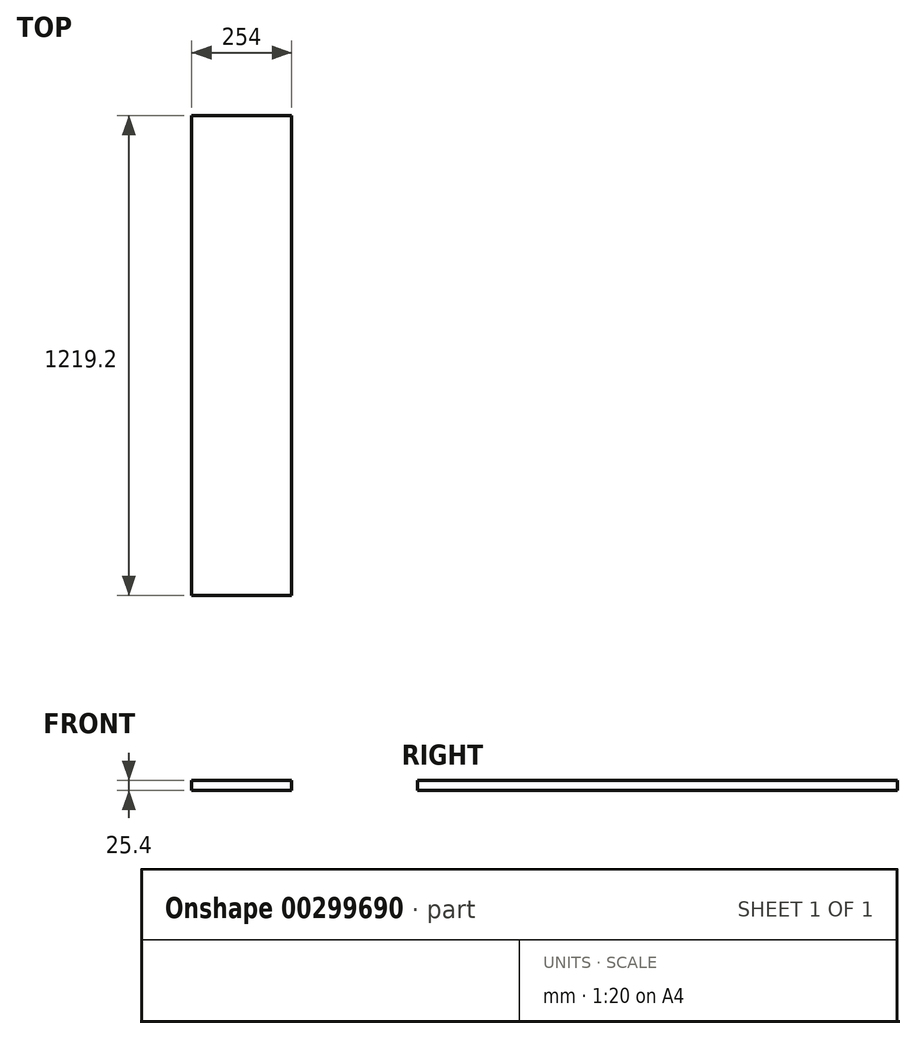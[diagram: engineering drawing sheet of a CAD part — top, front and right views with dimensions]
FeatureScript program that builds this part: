
annotation { "Feature Type Name" : "Feature", "Feature Type Description" : "" }
export const myFeature = defineFeature(function(context is Context, id is Id, definition is map)
    precondition{}
    {
        {
            var Q0;
            Q0=qCreatedBy(makeId("Top.planeOp"),FACE);
            var sketch = newSketch(context, id + "F0", { "sketchPlane" : qUnion([Q0])});
            skLineSegment(sketch, "E0.bottom", {"start": v(-128.89, 936.06) * mm, "end": v(125.11, 936.06) * mm});
            skLineSegment(sketch, "E0.top", {"start": v(-128.89, -283.14) * mm, "end": v(125.11, -283.14) * mm});
            skLineSegment(sketch, "E0.left", {"start": v(-128.89, 936.06) * mm, "end": v(-128.89, -283.14) * mm});
            skLineSegment(sketch, "E0.right", {"start": v(125.11, 936.06) * mm, "end": v(125.11, -283.14) * mm});
            skSolve(sketch);
        }
        {
            var Q0;
            Q0 = qSketchRegion(id + "F0", true);
            extrude(context, id + "F1", {"entities" : qUnion([Q0]), "depth" : 25.4 * mm});
        }
    });
